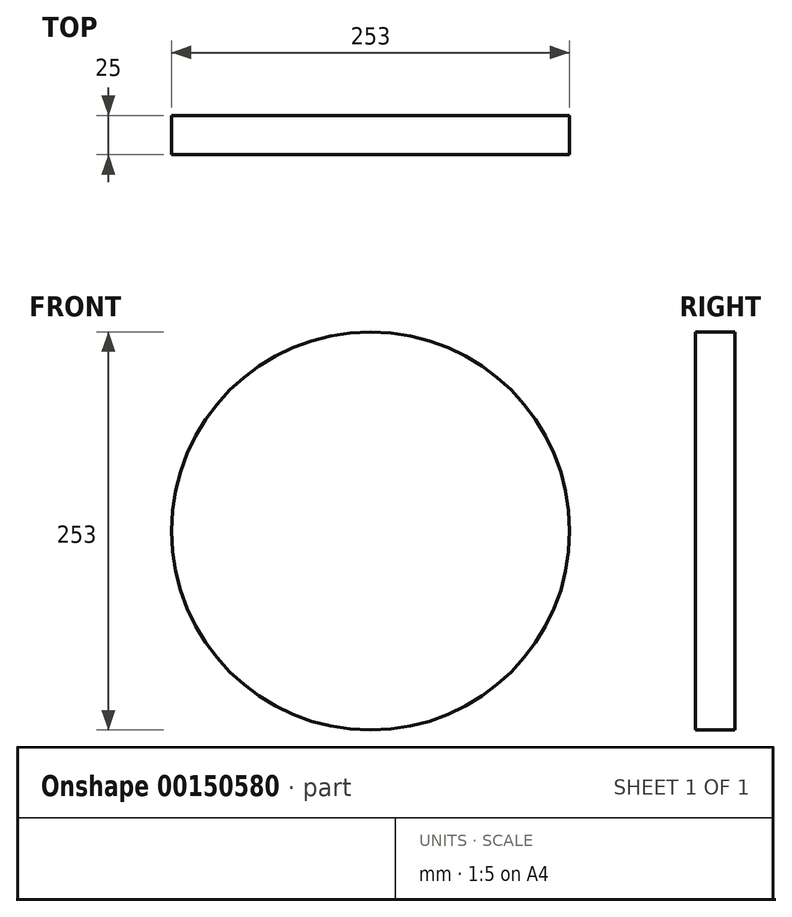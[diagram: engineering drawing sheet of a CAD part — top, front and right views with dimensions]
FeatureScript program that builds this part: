
annotation { "Feature Type Name" : "Feature", "Feature Type Description" : "" }
export const myFeature = defineFeature(function(context is Context, id is Id, definition is map)
    precondition{}
    {
        {
            var Q0;
            Q0=qCreatedBy(makeId("Front.planeOp"),FACE);
            var sketch = newSketch(context, id + "F0", { "sketchPlane" : qUnion([Q0])});
            skCircle(sketch, "E0", {"center": v(0, 0) * mm, "radius": 126.5 * mm});
            skSolve(sketch);
        }
        {
            var Q0;
            Q0 = qSketchRegion(id + "F0", true);
            extrude(context, id + "F1", {"entities" : qUnion([Q0]), "depth" : 25 * mm});
        }
    });
